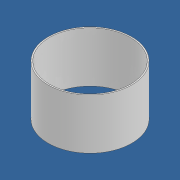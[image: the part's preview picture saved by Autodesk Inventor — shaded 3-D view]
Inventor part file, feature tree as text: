
AUTODESK INVENTOR PART (.ipt)
format: ipt  version: 2021 (Build 250183000, 183)  size: 82,944 bytes
history: native  units: in
note: dims shown in document units (in); Inventor stores cm internally (conversion verified against a paired STEP export)
features: extrude x1, sketch x1
ambient origin geometry x8: Origin, YZ Plane, XZ Plane, XY Plane, X Axis, Y Axis, Z Axis, Center Point
bodies: Solid1 (feature_tree)
feature tree (2):
  extrude  "Extrusion1"  Depth=5.9843in
  sketch  "Sketch1"  dims[d0=9.91in d1=9.6in d2=5.9843in d3=0.0in]
